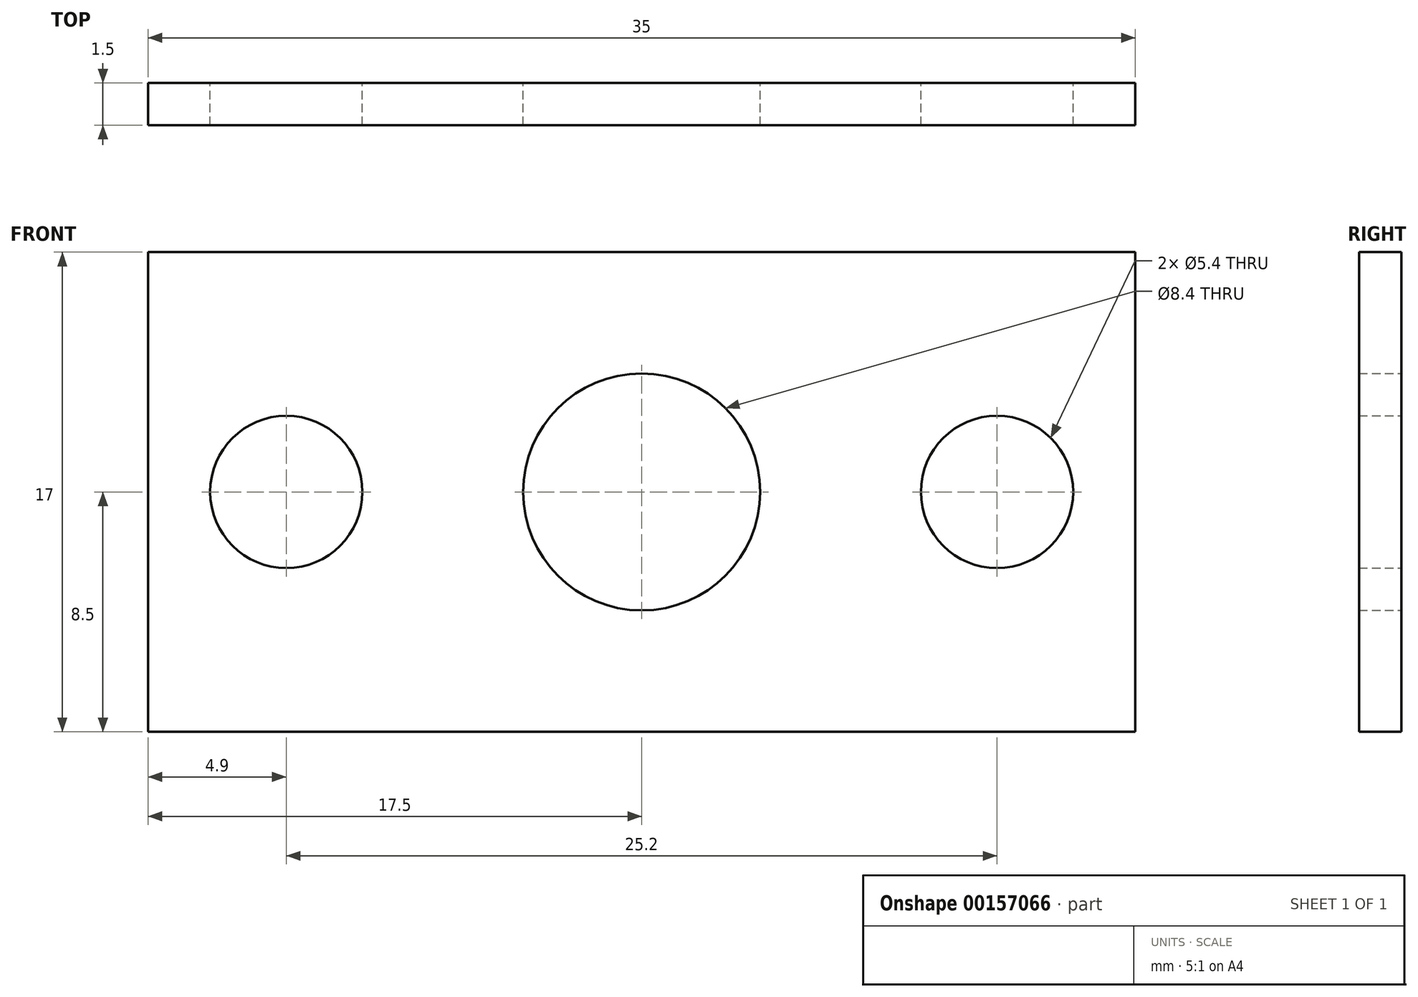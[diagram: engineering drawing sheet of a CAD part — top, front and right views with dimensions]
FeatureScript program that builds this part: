
annotation { "Feature Type Name" : "Feature", "Feature Type Description" : "" }
export const myFeature = defineFeature(function(context is Context, id is Id, definition is map)
    precondition{}
    {
        {
            var Q0;
            Q0=qCreatedBy(makeId("Front.planeOp"),FACE);
            var sketch = newSketch(context, id + "F0", { "sketchPlane" : qUnion([Q0])});
            skLineSegment(sketch, "E0.bottom", {"start": v(-17.5, -8.5) * mm, "end": v(17.5, -8.5) * mm});
            skLineSegment(sketch, "E0.top", {"start": v(-17.5, 8.5) * mm, "end": v(17.5, 8.5) * mm});
            skLineSegment(sketch, "E0.left", {"start": v(-17.5, -8.5) * mm, "end": v(-17.5, 8.5) * mm});
            skLineSegment(sketch, "E0.right", {"start": v(17.5, -8.5) * mm, "end": v(17.5, 8.5) * mm});
            skPoint(sketch, "E0.middle", {"position": v(0, 0) * mm});
            skCircle(sketch, "E1", {"center": v(0, 0) * mm, "radius": 4.2 * mm});
            skCircle(sketch, "E2", {"center": v(12.6, 0) * mm, "radius": 2.7 * mm});
            skCircle(sketch, "E3.MirrorC", {"center": v(-12.6, 0) * mm, "radius": 2.7 * mm});
            skSolve(sketch);
        }
        {
            var Q0;
            Q0 = qSketchRegion(id + "F0", true);
            extrude(context, id + "F1", {"entities" : qUnion([Q0]), "depth" : 1.5 * mm});
        }
    });
